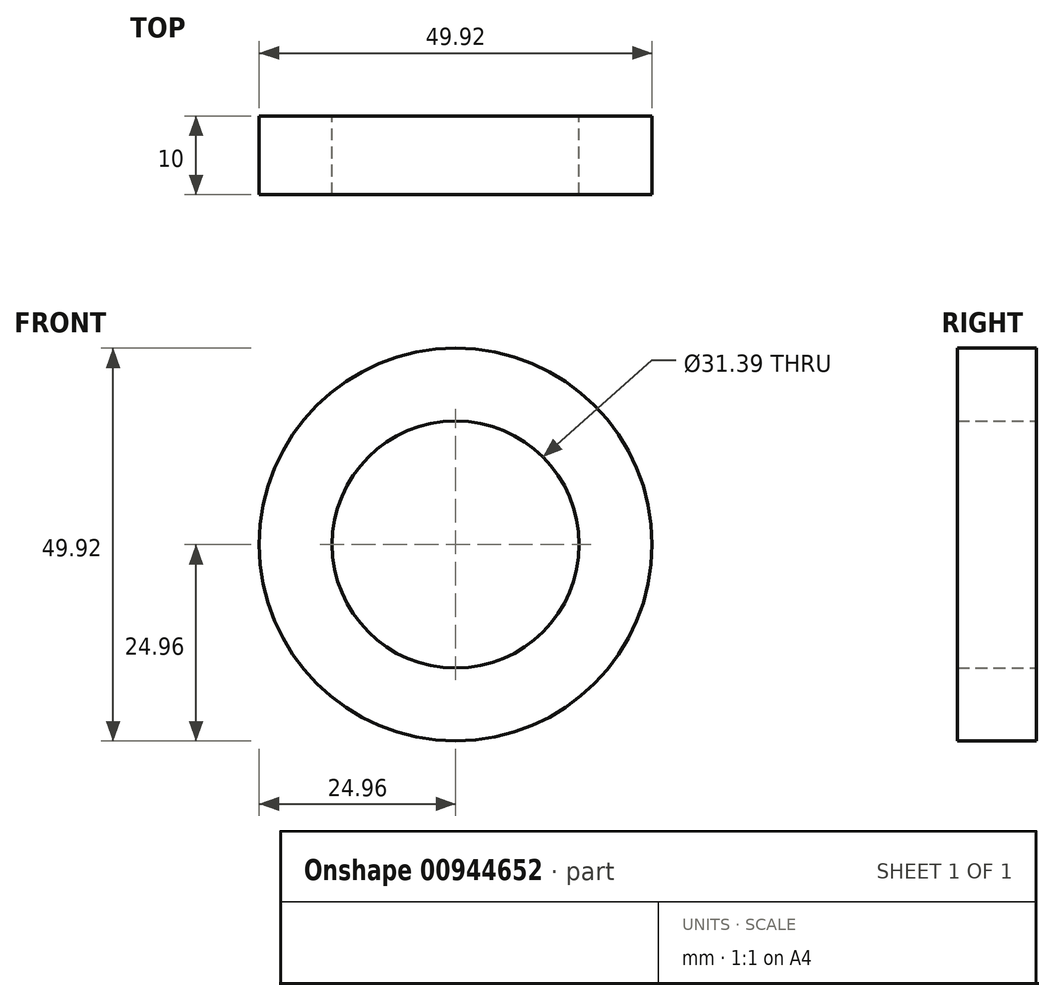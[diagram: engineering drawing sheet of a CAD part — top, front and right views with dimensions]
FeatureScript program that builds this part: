
annotation { "Feature Type Name" : "Feature", "Feature Type Description" : "" }
export const myFeature = defineFeature(function(context is Context, id is Id, definition is map)
    precondition{}
    {
        {
            var Q0;
            Q0=qCreatedBy(makeId("Front.planeOp"),FACE);
            var sketch = newSketch(context, id + "F0", { "sketchPlane" : qUnion([Q0])});
            skLineSegment(sketch, "E0", {"start": v(-20.09, 13.05) * mm, "end": v(-9.73, 13.05) * mm});
            skLineSegment(sketch, "E1.1.0", {"start": v(-23.92, -1.25) * mm, "end": v(-15.54, 4.84) * mm});
            skLineSegment(sketch, "E1.2.0", {"start": v(-18.61, -15.07) * mm, "end": v(-15.41, -5.22) * mm});
            skLineSegment(sketch, "E1.3.0", {"start": v(-6.2, -23.14) * mm, "end": v(-9.4, -13.28) * mm});
            skLineSegment(sketch, "E1.4.0", {"start": v(8.58, -22.36) * mm, "end": v(0.2, -16.27) * mm});
            skLineSegment(sketch, "E1.5.0", {"start": v(20.09, -13.05) * mm, "end": v(9.73, -13.05) * mm});
            skLineSegment(sketch, "E1.6.0", {"start": v(23.92, 1.25) * mm, "end": v(15.54, -4.84) * mm});
            skLineSegment(sketch, "E1.7.0", {"start": v(18.61, 15.07) * mm, "end": v(15.41, 5.22) * mm});
            skLineSegment(sketch, "E1.8.0", {"start": v(6.2, 23.14) * mm, "end": v(9.4, 13.28) * mm});
            skLineSegment(sketch, "E1.9.0", {"start": v(-8.58, 22.36) * mm, "end": v(-0.2, 16.27) * mm});
            skPoint(sketch, "E1.center", {"position": v(0, 0) * mm});
            skCircle(sketch, "E2", {"center": v(0, 0) * mm, "radius": 24.96 * mm});
            skCircle(sketch, "E3", {"center": v(0, 0) * mm, "radius": 10.9 * mm});
            skCircle(sketch, "E4", {"center": v(0, 0) * mm, "radius": 15.7 * mm});
            skSolve(sketch);
        }
        {
            var Q0;
            Q0 = qSketchRegion(id + "F0", true);
            extrude(context, id + "F1", {"entities" : qUnion([Q0]), "endBound" : BoundingType.SYMMETRIC, "depth" : 10 * mm, "offsetDistance" : 25.4 * mm});
        }
    });
